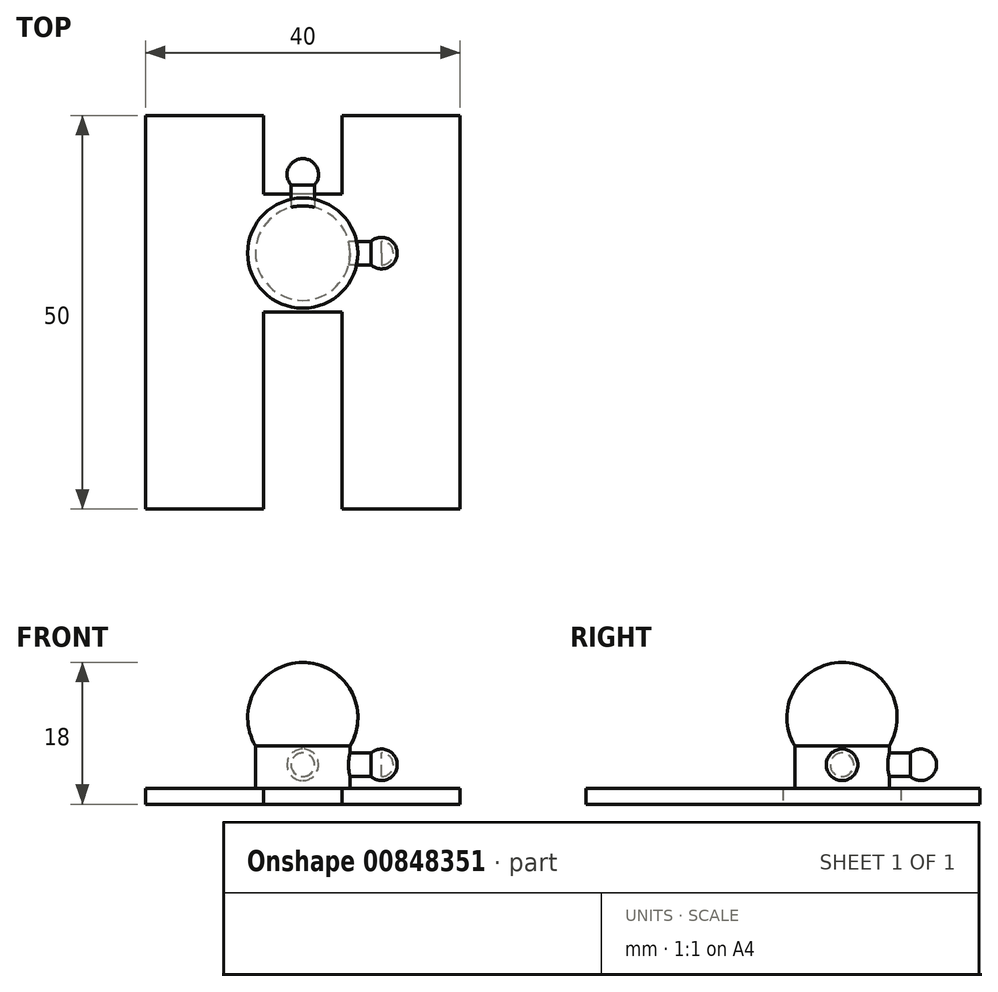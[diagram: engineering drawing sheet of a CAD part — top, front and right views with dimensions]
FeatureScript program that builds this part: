
annotation { "Feature Type Name" : "Feature", "Feature Type Description" : "" }
export const myFeature = defineFeature(function(context is Context, id is Id, definition is map)
    precondition{}
    {
        {
            var Q0;
            Q0=qCreatedBy(makeId("Top.planeOp"),FACE);
            var sketch = newSketch(context, id + "F0", { "sketchPlane" : qUnion([Q0])});
            skLineSegment(sketch, "E0", {"start": v(-20, 17.5) * mm, "end": v(-20, -32.5) * mm});
            skLineSegment(sketch, "E1", {"start": v(-20, -32.5) * mm, "end": v(-5, -32.5) * mm});
            skLineSegment(sketch, "E2", {"start": v(-5, -32.5) * mm, "end": v(-5, -7.5) * mm});
            skLineSegment(sketch, "E3", {"start": v(-5, -7.5) * mm, "end": v(5, -7.5) * mm});
            skLineSegment(sketch, "E4", {"start": v(5, -7.5) * mm, "end": v(5, -32.5) * mm});
            skLineSegment(sketch, "E5", {"start": v(5, -32.5) * mm, "end": v(20, -32.5) * mm});
            skLineSegment(sketch, "E6", {"start": v(20, -32.5) * mm, "end": v(20, 17.5) * mm});
            skLineSegment(sketch, "E7", {"start": v(20, 17.5) * mm, "end": v(5, 17.5) * mm});
            skLineSegment(sketch, "E8", {"start": v(5, 17.5) * mm, "end": v(5, 7.5) * mm});
            skLineSegment(sketch, "E9", {"start": v(5, 7.5) * mm, "end": v(-5, 7.5) * mm});
            skLineSegment(sketch, "E10", {"start": v(-5, 7.5) * mm, "end": v(-5, 17.5) * mm});
            skLineSegment(sketch, "E11", {"start": v(-5, 17.5) * mm, "end": v(-20, 17.5) * mm});
            skSolve(sketch);
        }
        {
            var Q0;
            Q0=makeQuery(id+"F0.imprint","IMPRINT",FACE,{"disambiguationData":[TD([[makeQuery(id+"F0.imprint","IMPRINT",EDGE,{"derivedFrom":sQuery(id+"F0.wireOp",EDGE,"E0")}),1.0]])]});
            extrude(context, id + "F1", {"entities" : qUnion([Q0]), "depth" : 2 * mm, "offsetDistance" : 25 * mm});
        }
        {
            var Q0;
            Q0=makeQuery(id+"F1.opExtrude","CAP_FACE",FACE,{"disambiguationData":[OSD([sQuery(id+"F0.wireOp",EDGE,"E0"),sQuery(id+"F0.wireOp",EDGE,"E1"),sQuery(id+"F0.wireOp",EDGE,"E2"),sQuery(id+"F0.wireOp",EDGE,"E3"),sQuery(id+"F0.wireOp",EDGE,"E4"),sQuery(id+"F0.wireOp",EDGE,"E5"),sQuery(id+"F0.wireOp",EDGE,"E6"),sQuery(id+"F0.wireOp",EDGE,"E7"),sQuery(id+"F0.wireOp",EDGE,"E8"),sQuery(id+"F0.wireOp",EDGE,"E9"),sQuery(id+"F0.wireOp",EDGE,"E10"),sQuery(id+"F0.wireOp",EDGE,"E11")])],"isStart":false});
            var sketch = newSketch(context, id + "F2", { "sketchPlane" : qUnion([Q0])});
            skCircle(sketch, "E12", {"center": v(0, 0) * mm, "radius": 6 * mm});
            skSolve(sketch);
        }
        {
            var Q0;
            Q0 = qSketchRegion(id + "F2", true);
            extrude(context, id + "F3", {"entities" : qUnion([Q0]), "operationType" : NewBodyOperationType.ADD, "depth" : 7.5 * mm, "offsetDistance" : 25 * mm});
        }
        {
            var Q0;
            Q0=qCreatedBy(makeId("Front.planeOp"),FACE);
            var sketch = newSketch(context, id + "F4", { "sketchPlane" : qUnion([Q0])});
            skLineSegment(sketch, "E13", {"start": v(0, 18) * mm, "end": v(0, 4) * mm});
            skArc(sketch, "E14", {"start": v(0, 18) * mm, "mid": v(-7, 11) * mm, "end": v(0, 4) * mm});
            skSolve(sketch);
        }
        {
            var Q0;
            {var subQ0=sQuery(id+"F4.wireOp",EDGE,"E13");Q0=makeQuery(id+"F4.imprint","IMPRINT",FACE,{"disambiguationData":[TD([[makeQuery(id+"F4.imprint","IMPRINT",EDGE,{"derivedFrom":subQ0}),-1.0]])]});}
            var Q1;
            Q1=sQuery(id+"F4.wireOp",EDGE,"E13");
            revolve(context, id + "F5", {"operationType" : NewBodyOperationType.ADD, "surfaceOperationType" : NewSurfaceOperationType.NEW, "entities" : qUnion([Q0]), "axis" : qUnion([Q1]), "revolveType" : RevolveType.FULL});
        }
        {
            var Q0;
            Q0=qCreatedBy(makeId("Right.planeOp"),FACE);
            var sketch = newSketch(context, id + "F6", { "sketchPlane" : qUnion([Q0])});
            skCircle(sketch, "E15", {"center": v(0, 5) * mm, "radius": 1.5 * mm});
            skSolve(sketch);
        }
        {
            var Q0;
            Q0 = qSketchRegion(id + "F6", true);
            extrude(context, id + "F7", {"entities" : qUnion([Q0]), "operationType" : NewBodyOperationType.ADD, "depth" : 10 * mm, "offsetDistance" : 25 * mm, "hasSecondDirection" : true, "secondDirectionOppositeDirection" : false, "secondDirectionDepth" : 5 * mm});
        }
        {
            var Q0;
            Q0=makeQuery(id+"F7.opExtrude","CAP_FACE",FACE,{"disambiguationData":[OSD([sQuery(id+"F6.wireOp",EDGE,"E15")])],"isStart":false});
            var sketch = newSketch(context, id + "F8", { "sketchPlane" : qUnion([Q0])});
            skLineSegment(sketch, "E16", {"start": v(0, 3) * mm, "end": v(0, 7) * mm});
            skArc(sketch, "E17", {"start": v(0, 3) * mm, "mid": v(2, 5) * mm, "end": v(0, 7) * mm});
            skSolve(sketch);
        }
        {
            var Q0;
            {var subQ0=sQuery(id+"F8.wireOp",EDGE,"E17");Q0=makeQuery(id+"F8.imprint","IMPRINT",FACE,{"disambiguationData":[TD([[makeQuery(id+"F8.imprint","IMPRINT",EDGE,{"derivedFrom":subQ0}),1.0]])]});}
            var Q1;
            Q1=sQuery(id+"F8.wireOp",EDGE,"E16");
            revolve(context, id + "F9", {"operationType" : NewBodyOperationType.ADD, "surfaceOperationType" : NewSurfaceOperationType.NEW, "entities" : qUnion([Q0]), "axis" : qUnion([Q1]), "revolveType" : RevolveType.FULL});
        }
        {
            var Q0;
            Q0=qCreatedBy(makeId("Front.planeOp"),FACE);
            var sketch = newSketch(context, id + "F10", { "sketchPlane" : qUnion([Q0])});
            skCircle(sketch, "E18", {"center": v(0, 5) * mm, "radius": 1.5 * mm});
            skSolve(sketch);
        }
        {
            var Q0;
            Q0 = qSketchRegion(id + "F10", true);
            extrude(context, id + "F11", {"entities" : qUnion([Q0]), "operationType" : NewBodyOperationType.ADD, "oppositeDirection" : true, "depth" : 10 * mm, "offsetDistance" : 25 * mm, "hasSecondDirection" : true, "secondDirectionOppositeDirection" : true, "secondDirectionDepth" : 5 * mm});
        }
        {
            var Q0;
            Q0=makeQuery(id+"F11.opExtrude","CAP_FACE",FACE,{"disambiguationData":[OSD([sQuery(id+"F10.wireOp",EDGE,"E18")])],"isStart":false});
            var sketch = newSketch(context, id + "F12", { "sketchPlane" : qUnion([Q0])});
            skLineSegment(sketch, "E19", {"start": v(0, 7) * mm, "end": v(0, 3) * mm});
            skArc(sketch, "E20", {"start": v(0, 3) * mm, "mid": v(2, 5) * mm, "end": v(0, 7) * mm});
            skSolve(sketch);
        }
        {
            var Q0;
            {var subQ0=sQuery(id+"F12.wireOp",EDGE,"E20");Q0=makeQuery(id+"F12.imprint","IMPRINT",FACE,{"disambiguationData":[TD([[makeQuery(id+"F12.imprint","IMPRINT",EDGE,{"derivedFrom":subQ0}),1.0]])]});}
            var Q1;
            {var subQ0=sQuery(id+"F12.wireOp",EDGE,"E19");var subQ1=makeQuery(id+"F11.opExtrude","CAP_EDGE",EDGE,{"disambiguationData":[OSD([sQuery(id+"F10.wireOp",EDGE,"E18")])],"isStart":false});var subQ2=makeQuery(id+"F12.imprint","INTERSECT",VERTEX,{"disambiguationData":[OD(0.0)],"derivedFrom":[subQ1,subQ0]});Q1=makeQuery(id+"F12.imprint","IMPRINT",FACE,{"disambiguationData":[TD([[makeQuery(id+"F12.imprint","IMPRINT",EDGE,{"disambiguationData":[TD([[subQ2,-1.0]])],"derivedFrom":subQ0}),1.0]])]});}
            var Q2;
            Q2=sQuery(id+"F12.wireOp",EDGE,"E19");
            revolve(context, id + "F13", {"operationType" : NewBodyOperationType.ADD, "surfaceOperationType" : NewSurfaceOperationType.NEW, "entities" : qUnion([Q0, Q1]), "axis" : qUnion([Q2]), "revolveType" : RevolveType.FULL});
        }
    });
